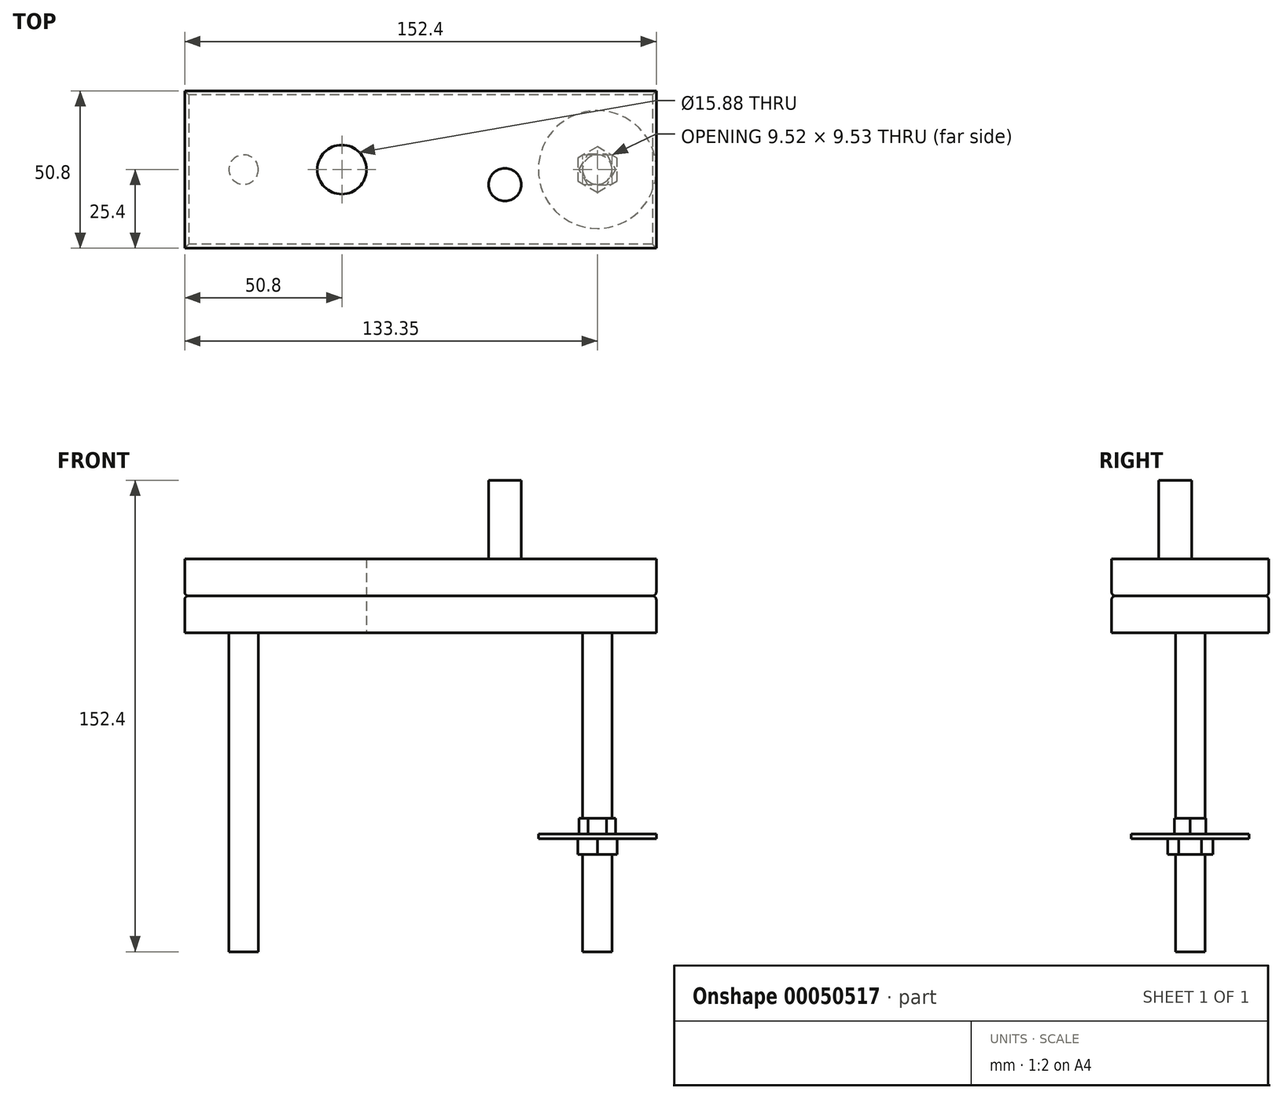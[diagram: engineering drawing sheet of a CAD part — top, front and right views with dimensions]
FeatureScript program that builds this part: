
annotation { "Feature Type Name" : "Feature", "Feature Type Description" : "" }
export const myFeature = defineFeature(function(context is Context, id is Id, definition is map)
    precondition{}
    {
        {
            var Q0;
            Q0=qCreatedBy(makeId("Top.planeOp"),FACE);
            var sketch = newSketch(context, id + "F0", { "sketchPlane" : qUnion([Q0])});
            skLineSegment(sketch, "E0.rect.bottom", {"start": v(76.2, 25.4) * mm, "end": v(-76.2, 25.4) * mm});
            skLineSegment(sketch, "E0.rect.top", {"start": v(76.2, -25.4) * mm, "end": v(-76.2, -25.4) * mm});
            skLineSegment(sketch, "E0.rect.left", {"start": v(76.2, 25.4) * mm, "end": v(76.2, -25.4) * mm});
            skLineSegment(sketch, "E0.rect.right", {"start": v(-76.2, 25.4) * mm, "end": v(-76.2, -25.4) * mm});
            skPoint(sketch, "E0.rect.middle", {"position": v(0, 0) * mm});
            skLineSegment(sketch, "E1.rect.bottom", {"start": v(57.15, 7.94) * mm, "end": v(-57.15, 7.94) * mm, "construction": true});
            skLineSegment(sketch, "E1.rect.top", {"start": v(57.15, -7.94) * mm, "end": v(-57.15, -7.94) * mm, "construction": true});
            skLineSegment(sketch, "E1.rect.left", {"start": v(57.15, 7.94) * mm, "end": v(57.15, -7.94) * mm, "construction": true});
            skLineSegment(sketch, "E1.rect.right", {"start": v(-57.15, 7.94) * mm, "end": v(-57.15, -7.94) * mm, "construction": true});
            skCircle(sketch, "E2", {"center": v(-25.4, 0) * mm, "radius": 7.94 * mm});
            skCircle(sketch, "E3", {"center": v(-57.15, 0) * mm, "radius": 4.76 * mm});
            skCircle(sketch, "E4", {"center": v(57.15, 0) * mm, "radius": 4.76 * mm});
            skSolve(sketch);
        }
        {
            var Q0;
            Q0 = qSketchRegion(id + "F0", true);
            extrude(context, id + "F1", {"entities" : qUnion([Q0]), "depth" : 12 * mm});
        }
        {
            var Q0;
            Q0=makeQuery(id+"F1.opExtrude","CAP_EDGE",EDGE,{"disambiguationData":[OSD([sQuery(id+"F0.wireOp",EDGE,"E0.rect.bottom")])],"isStart":true});
            var Q1;
            Q1=makeQuery(id+"F1.opExtrude","CAP_EDGE",EDGE,{"disambiguationData":[OSD([sQuery(id+"F0.wireOp",EDGE,"E0.rect.right")])],"isStart":true});
            var Q2;
            Q2=makeQuery(id+"F1.opExtrude","CAP_EDGE",EDGE,{"disambiguationData":[OSD([sQuery(id+"F0.wireOp",EDGE,"E0.rect.top")])],"isStart":true});
            var Q3;
            Q3=makeQuery(id+"F1.opExtrude","CAP_EDGE",EDGE,{"disambiguationData":[OSD([sQuery(id+"F0.wireOp",EDGE,"E0.rect.left")])],"isStart":true});
            fillet(context, id + "F2", {"entities" : qUnion([Q0, Q1, Q2, Q3]), "radius" : 1.27 * mm, "tangentPropagation" : true, "allowEdgeOverflow" : false});
        }
        {
            var Q0;
            Q0=makeQuery(id+"F1.opExtrude","SWEPT_BODY",BODY,{"disambiguationData":[OSD([sQuery(id+"F0.wireOp",EDGE,"E0.rect.bottom"),sQuery(id+"F0.wireOp",EDGE,"E0.rect.top"),sQuery(id+"F0.wireOp",EDGE,"E0.rect.left"),sQuery(id+"F0.wireOp",EDGE,"E0.rect.right"),sQuery(id+"F0.wireOp",EDGE,"8fbeb4ea-ec4f-4cc4-a0f0-a51186f15d0e"),sQuery(id+"F0.wireOp",EDGE,"fc65893b-e8cb-4b0e-abc0-7941c4b2c810"),sQuery(id+"F0.wireOp",EDGE,"659bfbd7-13c7-4a3c-918e-ecd252af4d11")])]});
            var Q1;
            Q1=qCreatedBy(makeId("Top.planeOp"),FACE);
            mirror(context, id + "F3", {"operationType" : NewBodyOperationType.ADD, "entities" : qUnion([Q0]), "mirrorPlane" : qUnion([Q1])});
        }
        {
            var Q0;
            Q0=makeQuery(id+"F1.opExtrude","CAP_FACE",FACE,{"disambiguationData":[OSD([sQuery(id+"F0.wireOp",EDGE,"E0.rect.bottom"),sQuery(id+"F0.wireOp",EDGE,"E0.rect.top"),sQuery(id+"F0.wireOp",EDGE,"E0.rect.left"),sQuery(id+"F0.wireOp",EDGE,"E0.rect.right"),sQuery(id+"F0.wireOp",EDGE,"E2"),sQuery(id+"F0.wireOp",EDGE,"E3"),sQuery(id+"F0.wireOp",EDGE,"E4")])],"isStart":false});
            var sketch = newSketch(context, id + "F4", { "sketchPlane" : qUnion([Q0])});
            skCircle(sketch, "E5", {"center": v(-57.15, 0) * mm, "radius": 4.76 * mm});
            skCircle(sketch, "E6", {"center": v(57.15, 0) * mm, "radius": 4.76 * mm});
            skSolve(sketch);
        }
        {
            var Q0;
            Q0 = qSketchRegion(id + "F4", true);
            extrude(context, id + "F5", {"entities" : qUnion([Q0]), "operationType" : NewBodyOperationType.ADD, "oppositeDirection" : true, "depth" : 76.2 * mm});
        }
        {
            var Q0;
            Q0=makeQuery(id+"F5.opExtrude","CAP_FACE",FACE,{"disambiguationData":[OSD([sQuery(id+"F4.wireOp",EDGE,"E6")])],"isStart":false});
            var sketch = newSketch(context, id + "F6", { "sketchPlane" : qUnion([Q0])});
            skCircle(sketch, "E7", {"center": v(57.15, 0) * mm, "radius": 4.76 * mm});
            skCircle(sketch, "E8", {"center": v(-57.15, 0) * mm, "radius": 4.76 * mm});
            skSolve(sketch);
        }
        {
            var Q0;
            Q0 = qSketchRegion(id + "F6", true);
            extrude(context, id + "F7", {"entities" : qUnion([Q0]), "operationType" : NewBodyOperationType.ADD, "depth" : 50.8 * mm});
        }
        {
            var Q0;
            Q0=makeQuery(id+"F7.opExtrude","CAP_FACE",FACE,{"disambiguationData":[OSD([sQuery(id+"F6.wireOp",EDGE,"E7")])],"isStart":false});
            cPlane(context, id + "F8", {"entities" : qUnion([Q0]), "cplaneType" : CPlaneType.OFFSET, "offset" : 38.1 * mm, "oppositeDirection" : true, "width" : 152.4 * mm, "height" : 152.4 * mm});
        }
        {
            var Q0;
            Q0=qCreatedBy(id+"F8.planeOp",FACE);
            var sketch = newSketch(context, id + "F9", { "sketchPlane" : qUnion([Q0])});
            skCircle(sketch, "E9", {"center": v(57.15, 0) * mm, "radius": 19.05 * mm});
            skSolve(sketch);
        }
        {
            var Q0;
            Q0 = qSketchRegion(id + "F9", true);
            extrude(context, id + "F10", {"entities" : qUnion([Q0]), "operationType" : NewBodyOperationType.ADD, "depth" : 1.52 * mm});
        }
        {
            var Q0;
            Q0=makeQuery(id+"F10.opExtrude","CAP_FACE",FACE,{"disambiguationData":[OSD([sQuery(id+"F9.wireOp",EDGE,"E9")])],"isStart":false});
            var sketch = newSketch(context, id + "F11", { "sketchPlane" : qUnion([Q0])});
            skCircle(sketch, "E10.cCircle", {"center": v(57.15, 0) * mm, "radius": 6.35 * mm, "construction": true});
            skLineSegment(sketch, "E10.0", {"start": v(57.15, 7.33) * mm, "end": v(63.5, 3.67) * mm});
            skLineSegment(sketch, "E10.1", {"start": v(63.5, 3.67) * mm, "end": v(63.5, -3.67) * mm});
            skLineSegment(sketch, "E10.2", {"start": v(63.5, -3.67) * mm, "end": v(57.15, -7.33) * mm});
            skLineSegment(sketch, "E10.3", {"start": v(57.15, -7.33) * mm, "end": v(50.8, -3.67) * mm});
            skLineSegment(sketch, "E10.4", {"start": v(50.8, -3.67) * mm, "end": v(50.8, 3.67) * mm});
            skLineSegment(sketch, "E10.5", {"start": v(50.8, 3.67) * mm, "end": v(57.15, 7.33) * mm});
            skPoint(sketch, "E10.0.midPoint", {"position": v(60.32, 5.5) * mm});
            skSolve(sketch);
        }
        {
            var Q0;
            Q0 = qSketchRegion(id + "F11", true);
            extrude(context, id + "F12", {"entities" : qUnion([Q0]), "operationType" : NewBodyOperationType.ADD, "depth" : 5.08 * mm});
        }
        {
            var Q0;
            Q0=makeQuery(id+"F10.opExtrude","CAP_FACE",FACE,{"disambiguationData":[OSD([sQuery(id+"F9.wireOp",EDGE,"E9")])],"isStart":true});
            var sketch = newSketch(context, id + "F13", { "sketchPlane" : qUnion([Q0])});
            skCircle(sketch, "E11.cCircle", {"center": v(57.15, 0) * mm, "radius": 5.08 * mm, "construction": true});
            skLineSegment(sketch, "E11.0", {"start": v(63.02, 0) * mm, "end": v(60.08, -5.08) * mm});
            skLineSegment(sketch, "E11.1", {"start": v(60.08, -5.08) * mm, "end": v(54.22, -5.08) * mm});
            skLineSegment(sketch, "E11.2", {"start": v(54.22, -5.08) * mm, "end": v(51.28, 0) * mm});
            skLineSegment(sketch, "E11.3", {"start": v(51.28, 0) * mm, "end": v(54.22, 5.08) * mm});
            skLineSegment(sketch, "E11.4", {"start": v(54.22, 5.08) * mm, "end": v(60.08, 5.08) * mm});
            skLineSegment(sketch, "E11.5", {"start": v(60.08, 5.08) * mm, "end": v(63.02, 0) * mm});
            skPoint(sketch, "E11.0.midPoint", {"position": v(61.55, -2.54) * mm});
            skSolve(sketch);
        }
        {
            var Q0;
            Q0 = qSketchRegion(id + "F13", true);
            extrude(context, id + "F14", {"entities" : qUnion([Q0]), "operationType" : NewBodyOperationType.ADD, "depth" : 5.08 * mm});
        }
        {
            var Q0;
            Q0=makeQuery(id+"F5.boolean.opBoolean","MERGE",FACE,{"derivedFrom":[makeQuery(id+"F1.opExtrude","CAP_FACE",FACE,{"disambiguationData":[OSD([sQuery(id+"F0.wireOp",EDGE,"E0.rect.bottom"),sQuery(id+"F0.wireOp",EDGE,"E0.rect.top"),sQuery(id+"F0.wireOp",EDGE,"E0.rect.left"),sQuery(id+"F0.wireOp",EDGE,"E0.rect.right"),sQuery(id+"F0.wireOp",EDGE,"E2"),sQuery(id+"F0.wireOp",EDGE,"E3"),sQuery(id+"F0.wireOp",EDGE,"E4")])],"isStart":false}),makeQuery(id+"F5.opExtrude","CAP_FACE",FACE,{"disambiguationData":[OSD([sQuery(id+"F4.wireOp",EDGE,"E5")])],"isStart":true}),makeQuery(id+"F5.opExtrude","CAP_FACE",FACE,{"disambiguationData":[OSD([sQuery(id+"F4.wireOp",EDGE,"E6")])],"isStart":true})]});
            var sketch = newSketch(context, id + "F15", { "sketchPlane" : qUnion([Q0])});
            skCircle(sketch, "E12", {"center": v(27.3, -4.87) * mm, "radius": 5.28 * mm});
            skSolve(sketch);
        }
        {
            var Q0;
            Q0 = qSketchRegion(id + "F15", true);
            extrude(context, id + "F16", {"entities" : qUnion([Q0]), "operationType" : NewBodyOperationType.ADD, "depth" : 25.4 * mm});
        }
    });
